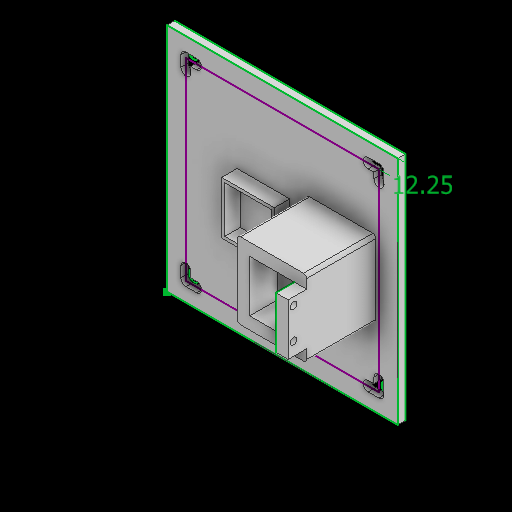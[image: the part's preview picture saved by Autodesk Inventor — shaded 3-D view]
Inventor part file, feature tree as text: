
AUTODESK INVENTOR PART (.ipt)
format: ipt  version: 2025.1 (Build 291241000, 241)  size: 285,696 bytes
history: native  units: in
note: dims shown in document units (in); Inventor stores cm internally (conversion verified against a paired STEP export)
features: sketch x16, extrude x9, projected_geometry x5, other x3, fillet x1
ambient origin geometry x8: Origin, YZ Plane, XZ Plane, XY Plane, X Axis, Y Axis, Z Axis, Center Point
bodies: Body1 (feature_tree)
feature tree (34):
  other  "솔리드1"
  extrude  "돌출1"  Depth=5.9055in
  sketch  "스케치2"
  extrude  "돌출3"  Depth=5.9055in
  sketch  "스케치8"
  sketch  "스케치9"
  sketch  "스케치10"
  extrude  "돌출7"  Depth=0.1969in TaperAngle=0.0deg
  extrude  "돌출8"  Depth=0.4823in
  extrude  "돌출9"  Depth=0.4823in
  extrude  "돌출10"  Depth=0.2559in
  extrude  "돌출11"  Depth=4.9409in
  sketch  "스케치16"
  sketch  "스케치17"
  extrude  "돌출12"  Depth=4.9409in
  sketch  "스케치19"
  fillet  "모깎기3"  Radius=0.1378in
  extrude  "돌출13"  Depth=0.2756in
  sketch  "스케치1"
  projected_geometry  "투영된 루프1"
  sketch  "스케치4"
  projected_geometry  "투영된 루프2"
  other  "스케치 - 직사각형 패턴3"
  other  "스케치 - 직사각형 패턴4"
  projected_geometry  "투영된 루프4"
  sketch  "스케치11"
  sketch  "스케치12"
  sketch  "스케치13"
  sketch  "스케치14"
  projected_geometry  "투영된 루프5"
  sketch  "스케치15"
  projected_geometry  "투영된 루프6"
  sketch  "스케치18"
  sketch  "스케치20"
